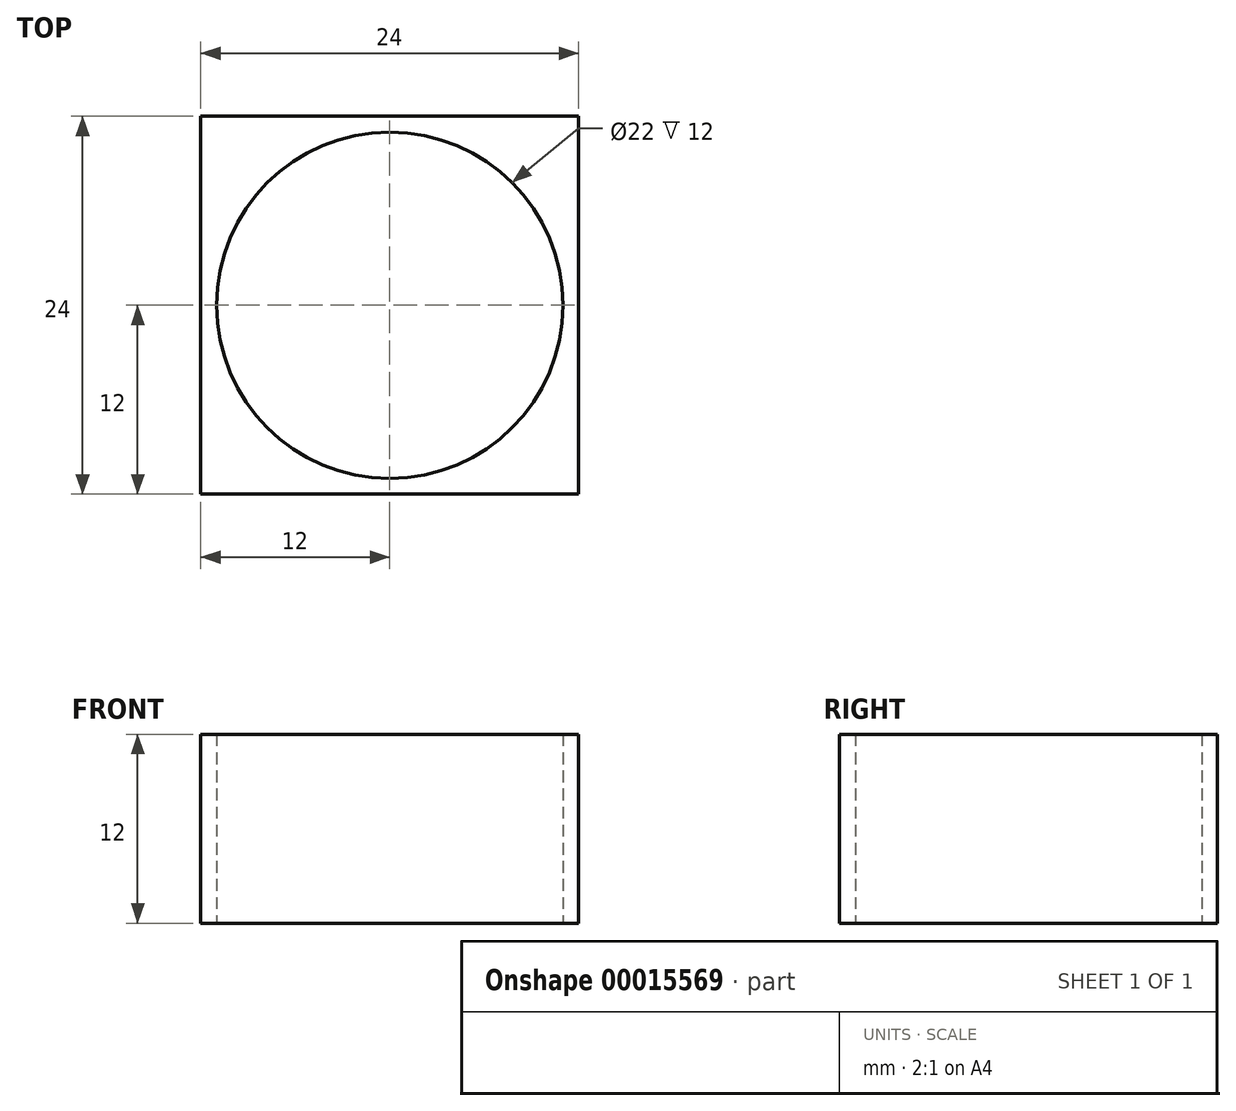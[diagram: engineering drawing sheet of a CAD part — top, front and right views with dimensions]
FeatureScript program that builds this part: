
annotation { "Feature Type Name" : "Feature", "Feature Type Description" : "" }
export const myFeature = defineFeature(function(context is Context, id is Id, definition is map)
    precondition{}
    {
        {
            var Q0;
            Q0=qCreatedBy(makeId("Top.planeOp"),FACE);
            var sketch = newSketch(context, id + "F0", { "sketchPlane" : qUnion([Q0])});
            skCircle(sketch, "E0", {"center": v(0, 0) * mm, "radius": 11 * mm});
            skLineSegment(sketch, "E1.rect.bottom", {"start": v(12, 12) * mm, "end": v(-12, 12) * mm});
            skLineSegment(sketch, "E1.rect.top", {"start": v(12, -12) * mm, "end": v(-12, -12) * mm});
            skLineSegment(sketch, "E1.rect.left", {"start": v(12, 12) * mm, "end": v(12, -12) * mm});
            skLineSegment(sketch, "E1.rect.right", {"start": v(-12, 12) * mm, "end": v(-12, -12) * mm});
            skSolve(sketch);
        }
        {
            var Q0;
            Q0=qSketchRegion(id+"F0",true);
            extrude(context, id + "F1", {"entities" : qUnion([Q0]), "depth" : 12 * mm});
        }
    });
